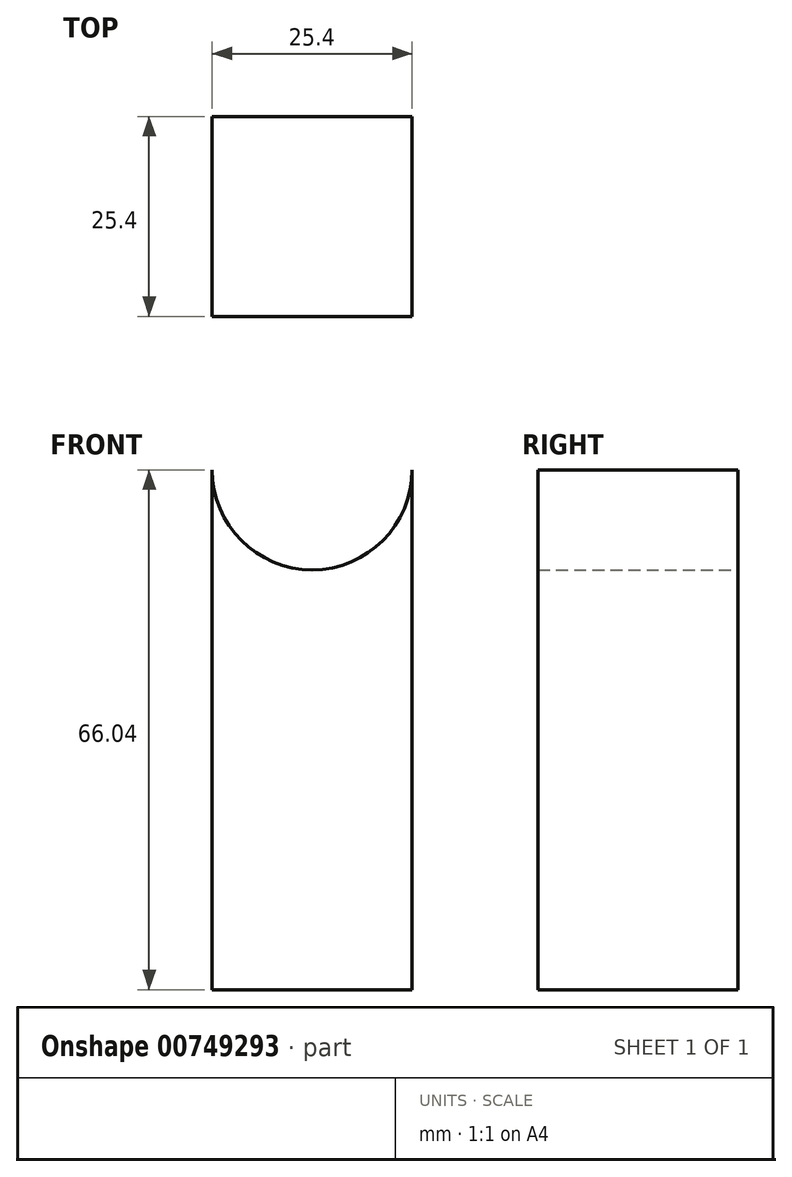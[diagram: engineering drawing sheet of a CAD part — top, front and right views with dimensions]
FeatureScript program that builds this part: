
annotation { "Feature Type Name" : "Feature", "Feature Type Description" : "" }
export const myFeature = defineFeature(function(context is Context, id is Id, definition is map)
    precondition{}
    {
        {
            var Q0;
            Q0=qCreatedBy(makeId("Front.planeOp"),FACE);
            var sketch = newSketch(context, id + "F0", { "sketchPlane" : qUnion([Q0])});
            skArc(sketch, "E0", {"start": v(-12.7, 0) * mm, "mid": v(0, -12.7) * mm, "end": v(12.7, 0) * mm});
            skPoint(sketch, "E1.start.orphan", {"position": v(-19.05, 0) * mm});
            skPoint(sketch, "E2.start.orphan", {"position": v(-19.05, -66.04) * mm});
            skPoint(sketch, "E3.end.orphan", {"position": v(12.7, -66.04) * mm});
            skPoint(sketch, "E4.trimOffspring.end.orphan", {"position": v(12.7, 0) * mm});
            skLineSegment(sketch, "E5", {"start": v(12.7, 0) * mm, "end": v(12.7, -66.04) * mm});
            skLineSegment(sketch, "E6", {"start": v(-12.7, 0) * mm, "end": v(-12.7, -66.04) * mm});
            skLineSegment(sketch, "E7", {"start": v(-12.7, -66.04) * mm, "end": v(12.7, -66.04) * mm});
            skSolve(sketch);
        }
        {
            var Q0;
            Q0 = qSketchRegion(id + "F0", true);
            extrude(context, id + "F1", {"entities" : qUnion([Q0]), "depth" : 25.4 * mm, "offsetDistance" : 25.4 * mm});
        }
    });
